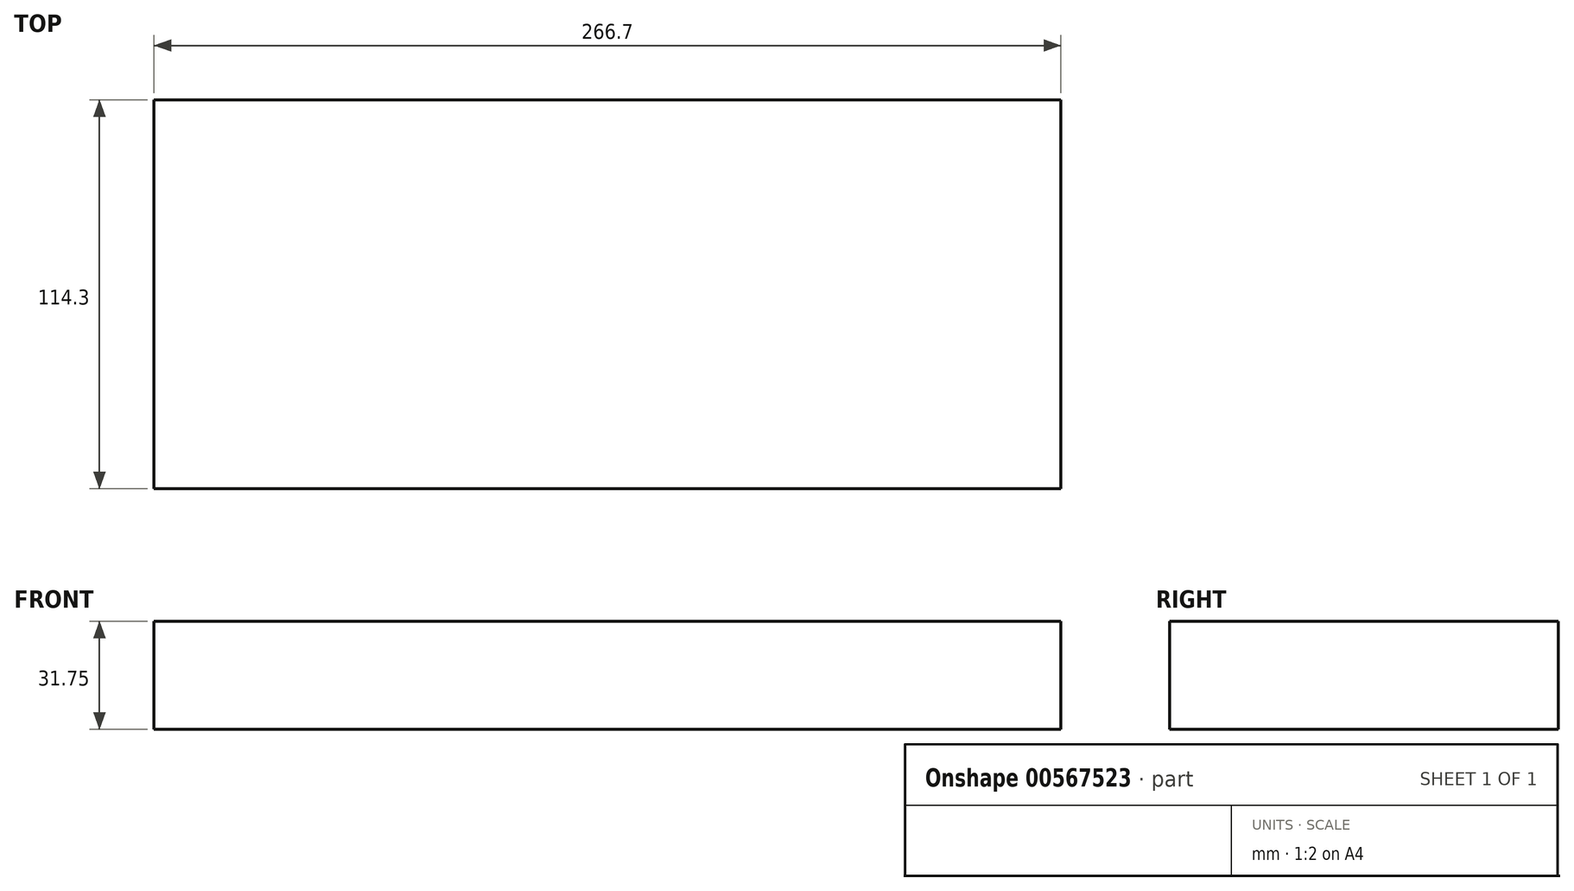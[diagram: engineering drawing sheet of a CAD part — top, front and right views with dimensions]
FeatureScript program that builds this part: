
annotation { "Feature Type Name" : "Feature", "Feature Type Description" : "" }
export const myFeature = defineFeature(function(context is Context, id is Id, definition is map)
    precondition{}
    {
        {
            var Q0;
            Q0=qCreatedBy(makeId("Top.planeOp"),FACE);
            var sketch = newSketch(context, id + "F0", { "sketchPlane" : qUnion([Q0])});
            skLineSegment(sketch, "E0", {"start": v(-133.35, 0) * mm, "end": v(-133.35, -57.15) * mm});
            skLineSegment(sketch, "E1.MirrorCS", {"start": v(-133.35, 0) * mm, "end": v(-133.35, 57.15) * mm});
            skLineSegment(sketch, "E2", {"start": v(-133.35, -57.15) * mm, "end": v(0, -57.15) * mm});
            skLineSegment(sketch, "E3", {"start": v(-133.35, 57.15) * mm, "end": v(0, 57.15) * mm});
            skLineSegment(sketch, "E4.MirrorCS", {"start": v(133.35, 57.15) * mm, "end": v(0, 57.15) * mm});
            skLineSegment(sketch, "E5.MirrorCS", {"start": v(133.35, 0) * mm, "end": v(133.35, 57.15) * mm});
            skLineSegment(sketch, "E6.MirrorCS", {"start": v(133.35, 0) * mm, "end": v(133.35, -57.15) * mm});
            skLineSegment(sketch, "E7.MirrorCS", {"start": v(133.35, -57.15) * mm, "end": v(0, -57.15) * mm});
            skSolve(sketch);
        }
        {
            var Q0;
            Q0 = qSketchRegion(id + "F0", true);
            extrude(context, id + "F1", {"entities" : qUnion([Q0]), "depth" : 31.75 * mm, "offsetDistance" : 25.4 * mm});
        }
    });
